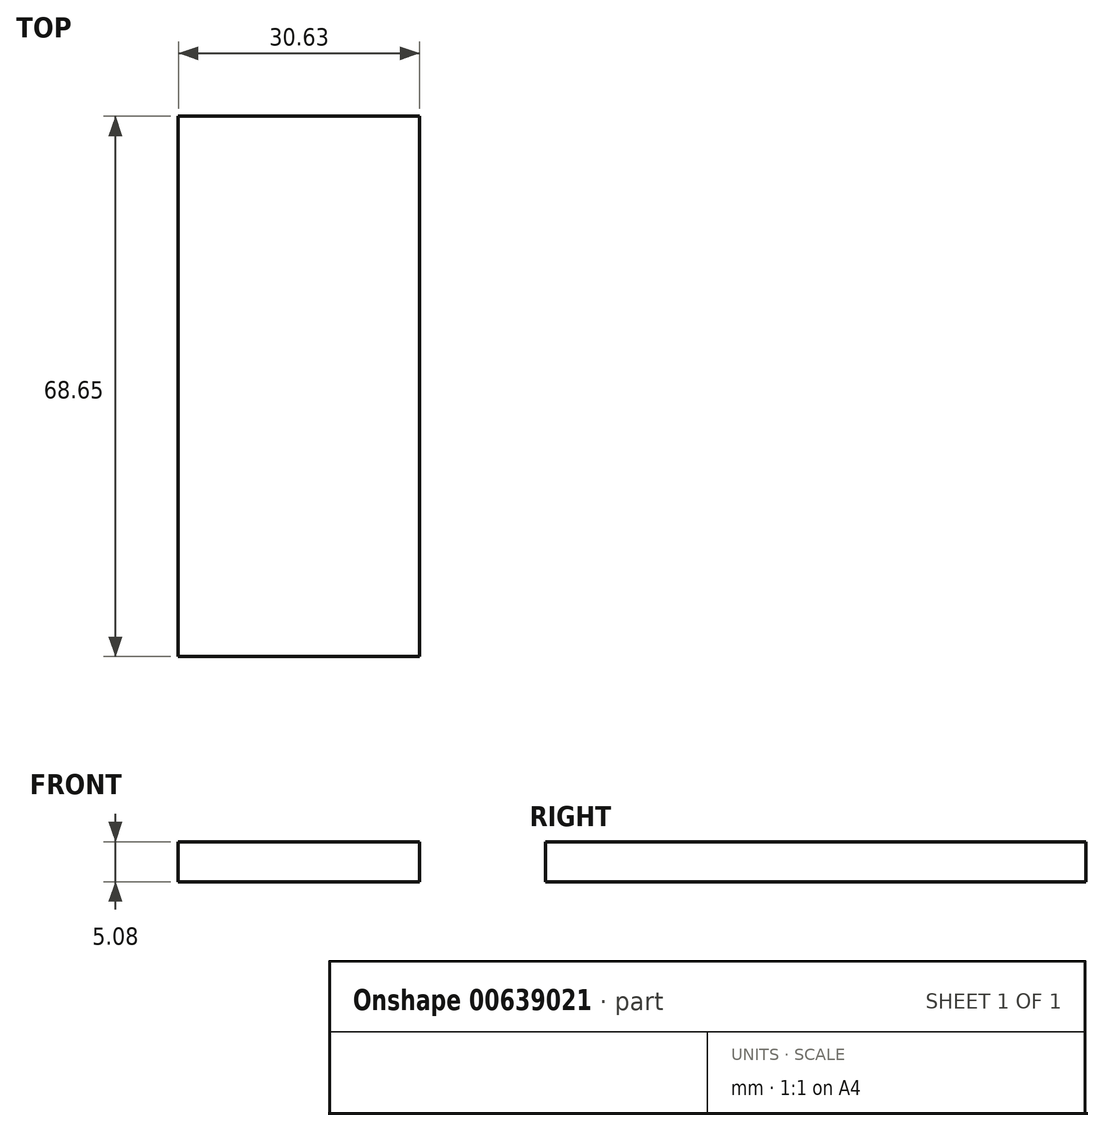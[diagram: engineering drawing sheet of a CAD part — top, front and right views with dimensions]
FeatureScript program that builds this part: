
annotation { "Feature Type Name" : "Feature", "Feature Type Description" : "" }
export const myFeature = defineFeature(function(context is Context, id is Id, definition is map)
    precondition{}
    {
        {
            var Q0;
            Q0=qCreatedBy(makeId("Top.planeOp"),FACE);
            var sketch = newSketch(context, id + "F0", { "sketchPlane" : qUnion([Q0])});
            skLineSegment(sketch, "E0.bottom", {"start": v(0, 0) * mm, "end": v(-30.63, 0) * mm});
            skLineSegment(sketch, "E0.top", {"start": v(0, -68.65) * mm, "end": v(-30.63, -68.65) * mm});
            skLineSegment(sketch, "E0.left", {"start": v(0, 0) * mm, "end": v(0, -68.65) * mm});
            skLineSegment(sketch, "E0.right", {"start": v(-30.63, 0) * mm, "end": v(-30.63, -68.65) * mm});
            skSolve(sketch);
        }
        {
            var Q0;
            Q0=makeQuery(id+"F0.imprint","IMPRINT",FACE,{"disambiguationData":[TD([[makeQuery(id+"F0.imprint","IMPRINT",EDGE,{"derivedFrom":sQuery(id+"F0.wireOp",EDGE,"E0.bottom")}),1.0]])]});
            extrude(context, id + "F1", {"entities" : qUnion([Q0]), "depth" : 5.08 * mm, "offsetDistance" : 25.4 * mm});
        }
        {
            var Q0;
            Q0=makeQuery(id+"F1.opExtrude","CAP_FACE",FACE,{"disambiguationData":[OSD([sQuery(id+"F0.wireOp",EDGE,"E0.bottom"),sQuery(id+"F0.wireOp",EDGE,"E0.top"),sQuery(id+"F0.wireOp",EDGE,"E0.left"),sQuery(id+"F0.wireOp",EDGE,"E0.right")])],"isStart":false});
            var sketch = newSketch(context, id + "F2", { "sketchPlane" : qUnion([Q0])});
            skSolve(sketch);
        }
        {
            var Q0;
            Q0=makeQuery(id+"F2.imprint","IMPRINT",FACE,{"disambiguationData":[TD([[makeQuery(id+"F2.imprint","IMPRINT",EDGE,{"derivedFrom":makeQuery(id+"F1.opExtrude","CAP_EDGE",EDGE,{"disambiguationData":[OSD([sQuery(id+"F0.wireOp",EDGE,"E0.bottom")])],"isStart":false})}),1.0]])]});
            var sketch = newSketch(context, id + "F3", { "sketchPlane" : qUnion([Q0])});
            skSolve(sketch);
        }
    });
